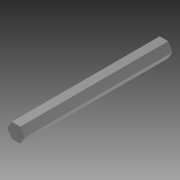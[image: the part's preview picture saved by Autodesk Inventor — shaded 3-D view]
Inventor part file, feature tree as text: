
AUTODESK INVENTOR PART (.ipt)
format: ipt  version: 2014 (Build 180170000, 170)  size: 102,400 bytes
history: native  units: in
note: dims shown in document units (in); Inventor stores cm internally (conversion verified against a paired STEP export)
features: extrude x1, sketch x1
ambient origin geometry x8: Origin, YZ Plane, XZ Plane, XY Plane, X Axis, Y Axis, Z Axis, Center Point
bodies: Solid1 (feature_tree)
feature tree (2):
  extrude  "Extrusion1"  Depth=5.0in TaperAngle=0.0deg
  sketch  "Sketch1"  dims[d0=0.5in d1=5.0in d2=0.0in]
